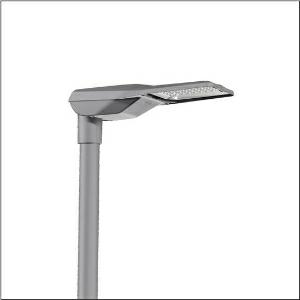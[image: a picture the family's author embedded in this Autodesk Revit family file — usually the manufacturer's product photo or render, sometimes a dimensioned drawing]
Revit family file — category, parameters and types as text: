
# Revit family: streetlight_sl_21_iq_mini___st0_5a_5xe2b31d08hb_2e1a
name_source: partatom
category: Lighting Fixtures
units: mm (PartAtom-declared; Revit-internal decimal feet)

## family parameters
Cut with Voids When Loaded = No
Host = Face
Light Source = No
Part Type = Normal
Room Calculation Point = No
Round Connector Dimension = Use Diameter
Shared = No

## types (1)
- --- (1 x LED, 9450 lm, 70.9 W, 3000K)
    Apparent Load = 71 VA
    CIE Flux Codes = 41 75 97 100 100
    Color Rendering = 70
    Color Temperature = 3000K
    Default Elevation = 1800 mm
    Description = Streetlight SL 21 iQ mini, mast luminaire, primary light control with lens, of PMMA, primary optical cover: cover, of toughened safety glass, transparent, light distribution: ST0.5a, light emission: direct distribution, primary light characteristic: asymmetric, installation type: post-top, side-entry, LED, High Power LED, rated luminous flux: 9.450lm, luminous efficacy: 133lm/W, light colour: 730, colour temperature: 3000K, control gear: iQ-Comfort, control: Auto-Match, Temp-Guard, Lumen-Switch, Night-Set, Smart-Wire, Light-Fading, Desk-Remote (wireless, voltage-free reading and setting of iQ features in the workshop via application-optimized NFC function/RFID function), optimised constant luminous flux control (CLO 2.0), pre-setting: linear dimming characteristic, mains connection: 220..240V, AC, 50/60Hz, start of lifetime: 71W, end of service life: 75W, reduction: 31W, luminaire housing, of diecast aluminium, powder-coated, SITECO metallic grey (DB 702S), corrosivity category C5 high according to DIN EN ISO 12944, please order mast flange separately, inclination adjustable: 0°, 5°, 10°, 15°, sealing non-destructively replaceable, multi-level sealing system, length: 628mm, width: 235mm, height: 110mm, mast flange for spigot size: 42mm (side-entry): 5XC10008XM4, 60/48mm (side-entry/post-top): 5XC10108XM2, 76/60mm (side-entry/post-top): 5XC10108XM1, mounting height: 4..8m, protection rating (complete): IP66, insulation class (complete): insulation class II (safety insulation), certification: CE, ENEC, ENEC+, VDE, impact resistance: IK10, permissible operating ambient temperature for outdoor applications: -40..+50°C, standard-compliant lighting for roads and squares, packaging unit: 1 piece

Light Distribution: ST0.5a
    Height = 110 mm
    Lamp = 1 x LED
    Lamp Light Flux = 9450 lm
    Lamp Power = 70.9 W
    Lamp count = 1
    Length = 625 mm
    Luminous efficacy = 133 lm/W
    Manufacturer = Siteco
    ModVariant = No
    Model = 5XE2B31D08HB
    Number of Poles = 1
    OnlyDefault = Yes
    Power Factor = 1
    Product Name = Streetlight SL 21 iQ mini | ST0.5a
    Product group = mast luminaire | pylon top
    ProductGroupID = 6100
    Protection Class = Protection class II
    Protection Degree = IP 66
    RLX_Detail_Level = 1
    RLX_Emergency_Light_Flux = 0 lm
    RLX_Emergency_Type = 0
    RLX_Emergency_Type_DB = No
    RlxData = <blob elided: 37317 chars, md5=be212925>
    Socket = socket
    Standby Power = 0 W
    System Light Flux = 9450 lm
    System Power = 71 W
    Type Comments = factory setting: luminous flux: 100 % | dim-lin: 254 | 711 mA
    Type Image = l_1003519.jpg
    URL = http://relux.com
    VarID = @adj_158097
    Voltage = 0 V
    Weight = 0.00 kg
    Width = 234 mm

## geometry (parser evidence)
native form markers: Blend x4, Sweep x10
no freeform markers — native parametric forms only
